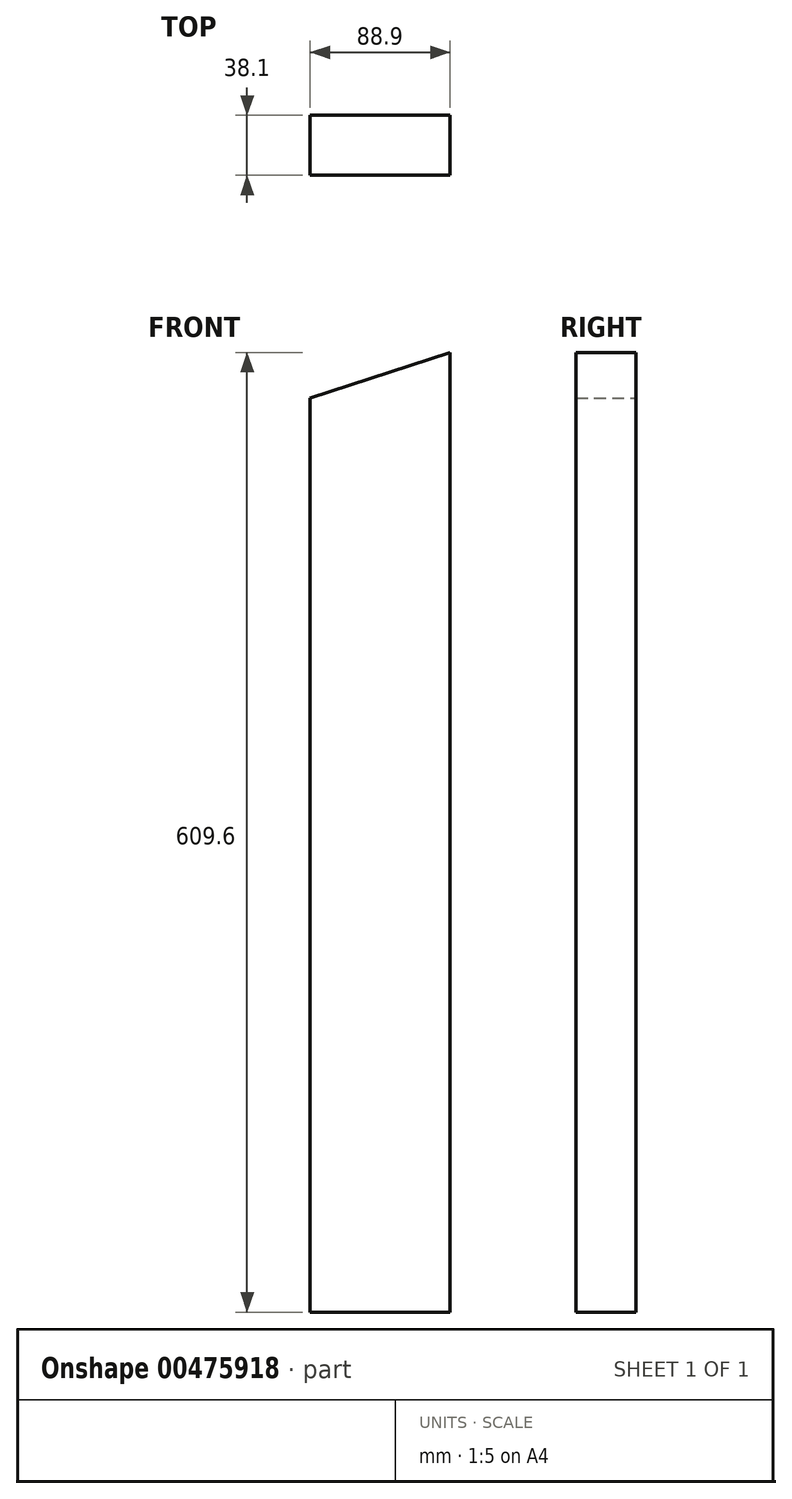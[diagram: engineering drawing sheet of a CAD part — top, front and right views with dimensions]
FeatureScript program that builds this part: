
annotation { "Feature Type Name" : "Feature", "Feature Type Description" : "" }
export const myFeature = defineFeature(function(context is Context, id is Id, definition is map)
    precondition{}
    {
        {
            var Q0;
            Q0=qCreatedBy(makeId("Front.planeOp"),FACE);
            var sketch = newSketch(context, id + "F0", { "sketchPlane" : qUnion([Q0])});
            skLineSegment(sketch, "E0.top", {"start": v(44.45, -304.8) * mm, "end": v(-44.45, -304.8) * mm});
            skLineSegment(sketch, "E0.left", {"start": v(44.45, 304.8) * mm, "end": v(44.45, -304.8) * mm});
            skLineSegment(sketch, "E0.right", {"start": v(-44.45, 275.92) * mm, "end": v(-44.45, -304.8) * mm});
            skPoint(sketch, "E0.middle", {"position": v(0, 0) * mm});
            skLineSegment(sketch, "E1", {"start": v(44.45, 304.8) * mm, "end": v(-44.45, 275.92) * mm});
            skSolve(sketch);
        }
        {
            var Q0;
            Q0 = qSketchRegion(id + "F0", true);
            extrude(context, id + "F1", {"entities" : qUnion([Q0]), "endBound" : BoundingType.SYMMETRIC, "depth" : 38.1 * mm, "offsetDistance" : 25.4 * mm});
        }
    });
